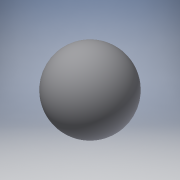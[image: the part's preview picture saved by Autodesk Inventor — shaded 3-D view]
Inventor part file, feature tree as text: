
AUTODESK INVENTOR PART (.ipt)
format: ipt  version: 2016 (Build 200138000, 138)  size: 117,248 bytes
history: native  units: in
note: dims shown in document units (in); Inventor stores cm internally (conversion verified against a paired STEP export)
features: revolve x1, sketch x1
ambient origin geometry x8: Origin, YZ Plane, XZ Plane, XY Plane, X Axis, Y Axis, Z Axis, Center Point
bodies: Solid1 (feature_tree)
feature tree (2):
  revolve  "Revolution1"  [1 undecoded]
  sketch  "Sketch1"  dims[d0=10.0in d2=5.0in d3=90.0deg]
note: 1 required parameter value undecoded (feature->parameter linkage not recoverable at this tier; creation-order binding heuristic only, values carry confidence <= 0.55)
